# Revit family: QF_ELECTROLUXPROFESSIONAL_1LSNTH_WS6-35_E
name_source: partatom
category: Attrezzature speciali
units: mm (PartAtom-declared; Revit-internal decimal feet)

## family parameters
Basato su piano di lavoro = No
Condiviso = No
Punto di calcolo locali = No
Quota connettore circolare = Usa diametro
Sempre verticale = Sì
Taglio con vuoti quando caricato = No
Tipo di parte = Normale

## types (14) — shared parameters
Depth = 1115.4 mm  [stored 3.65945 ft]
Depth Actual = 1115 mm  [stored 3.65814 ft]
Height = 1466.8 mm  [stored 4.81234 ft]
Height Actual = 1465 mm  [stored 4.80643 ft]
Latent Heat Output = 0.0
Length Actual = 910 mm  [stored 2.98556 ft]
Modello = WS6-35
Produttore = Electrolux Professional
Sensible Heat Output = 0.0
URL = www.electroluxprofessional.com
Weight = 307
Width = 910 mm  [stored 2.98556 ft]
zero-valued in all types: Gas KW, Prospetto di default, Steam Pounds per Hour

## per-type parameters (varying)
| type | Cycle | Descrizione | Item Number | Phase | Volts | Watts |
| 9868130296 | 50 Hz | WASHER WS6-35 35KG EL 19,1KW 380-400/50/3N COMPASS PRO 6G01 ML 2xWATER POWDER+5xLIQ. VALV.OPEN SST/SILVER 2.I/O DISCON. | 1LSPNC | 3 | 400 V | 20200 W |
| 9868130362 | 50 Hz | WASHER WS6-35 35KG EL 21KW 440/50/3 COMPASS PRO 6G01 ML 2xWATER POWDER+5xLIQ. VALV.CLOSED SST 2.I/O TRAFO DISCON. STOP | 1LT6CH | 3 | 440 V | 22200 W |
| 9868130313 | 50 Hz | WASHER WS6-35 35KG NO HEAT 220-240/50/1N COMPASS PRO 6G01 ML 2xWATER POWDER+5xLIQ. VALV.OPEN SILVER 2.I/O DISCON. STOP | 1LSPSG | 1 | 240 V | 1300 W |
| 9868130194 | 50 Hz | WASHER WS6-35 35KG MOP 23KW 415/50/3N COMPASS PRO 6M14 ML 2xWATER POWDER+5xLIQ. EL.VALV.OPEN SST/SILVER 2.I/O QC DISCON. | 1LA1DA | 3 | 415 V | 24100 W |
| 9868130289 | 50 Hz | WASHER WS6-35 35KG EL 19,1KW 380-400/50/3N COMPASS PRO 6G01 ML 2xWATER POWDER VALV.OPEN SILVER DISCON. STOP | 1LSPBZ | 3 | 400 V | 20200 W |
| 9868130343 | 50 Hz | WASHER WS6-35 35KG EL 19,8KW 415/50/3N COMPASS PRO 6G01 ML 2xWATER POWDER+5xLIQ. VALV.CLOSED SILVER 2.I/O DISCON. STOP | 1L82BY | 3 | 415 V | 20900 W |
| 9868130175 | 50 Hz | WASHER WS6-35 35KG EL 19,1KW 380-400/50/3N COMPASS PRO 6G01 ML 2xWATER POWDER+5xLIQ. VALV.OPEN SILVER 2.I/O DISCON. STOP | 1L0GCE | 3 | 400 V | 20200 W |
| 9868130191 | 50 Hz | WASHER WS6-35 35KG NO HEAT 200/50/60/3 COMPASS PRO 6L41 JP,EN 2xWATER 5xLIQ. VALV.OPEN SILVER 2.I/O DISCON. | 1LA1BD | 3 | 200 V | 1300 W |
| 9868130197 | 60 Hz | WASHER WS6-35 35KG NO HEAT 208-240/60/1 COMPASS PRO 6G01 ML 2xWATER POWDER+5xLIQ. VALV.CLOSED SILVER 2.I/O STOP | 1LSPB0 | 1 | 240 V | 1300 W |
| 9868130244 | 60 Hz | WASHER WS6-35 35KG NO HEAT 208-240/60/1 COMPASS PRO 6L01 ML 2xWATER POWDER+5xLIQ. VALV.OPEN SILVER ELS-NETW. 2.I/O | 1L0GNF | 1 | 240 V | 1300 W |
| 9868130238 | 60 Hz | WASHER WS6-35 35KG EL 21KW 440/60/3 COMPASS PRO 6G07 ML 2xWATER POWDER+5xLIQ. VALV.OPEN SILVER 2.I/O QC TRAFO DISCON. ST | 1L0GLS | 3 | 440 V | 22200 W |
| 9868130187 | 50 Hz | WASHER WS6-35 35KG EL 21KW 440/50/3 COMPASS PRO 6G01 ML 2xWATER POWDER+5xLIQ. VALV.OPEN SILVER 2.I/O TRAFO DISCON. STOP | 1LA1AN | 3 | 440 V | 22200 W |
| 9868130367 | 50 Hz | WASHER WS6-35 35KG EL 19,1KW 380-400/50/3N COMPASS PRO 6G01 ML 2xWATER POWDER+5xLIQ. VALV.OPEN SST 2.I/O DISCON. STOP | 1L0HJ4 | 3 | 400 V | 20200 W |
| 9868130271 | 50 Hz | WASHER WS6-35 35KG NO HEAT 200/50/60/3 COMPASS PRO 6L41 JP,EN 2xWATER POWDER+5xLIQ. VALV.OPEN SILVER 2.I/O DISCON. | 1L827T | 3 | 200 V | 1300 W |

note: [stored X ft] marks values corroborated as IEEE doubles in the binary element streams (Revit-internal decimal feet)

## geometry (parser evidence)
native form markers: Sweep x4
no freeform markers — native parametric forms only
